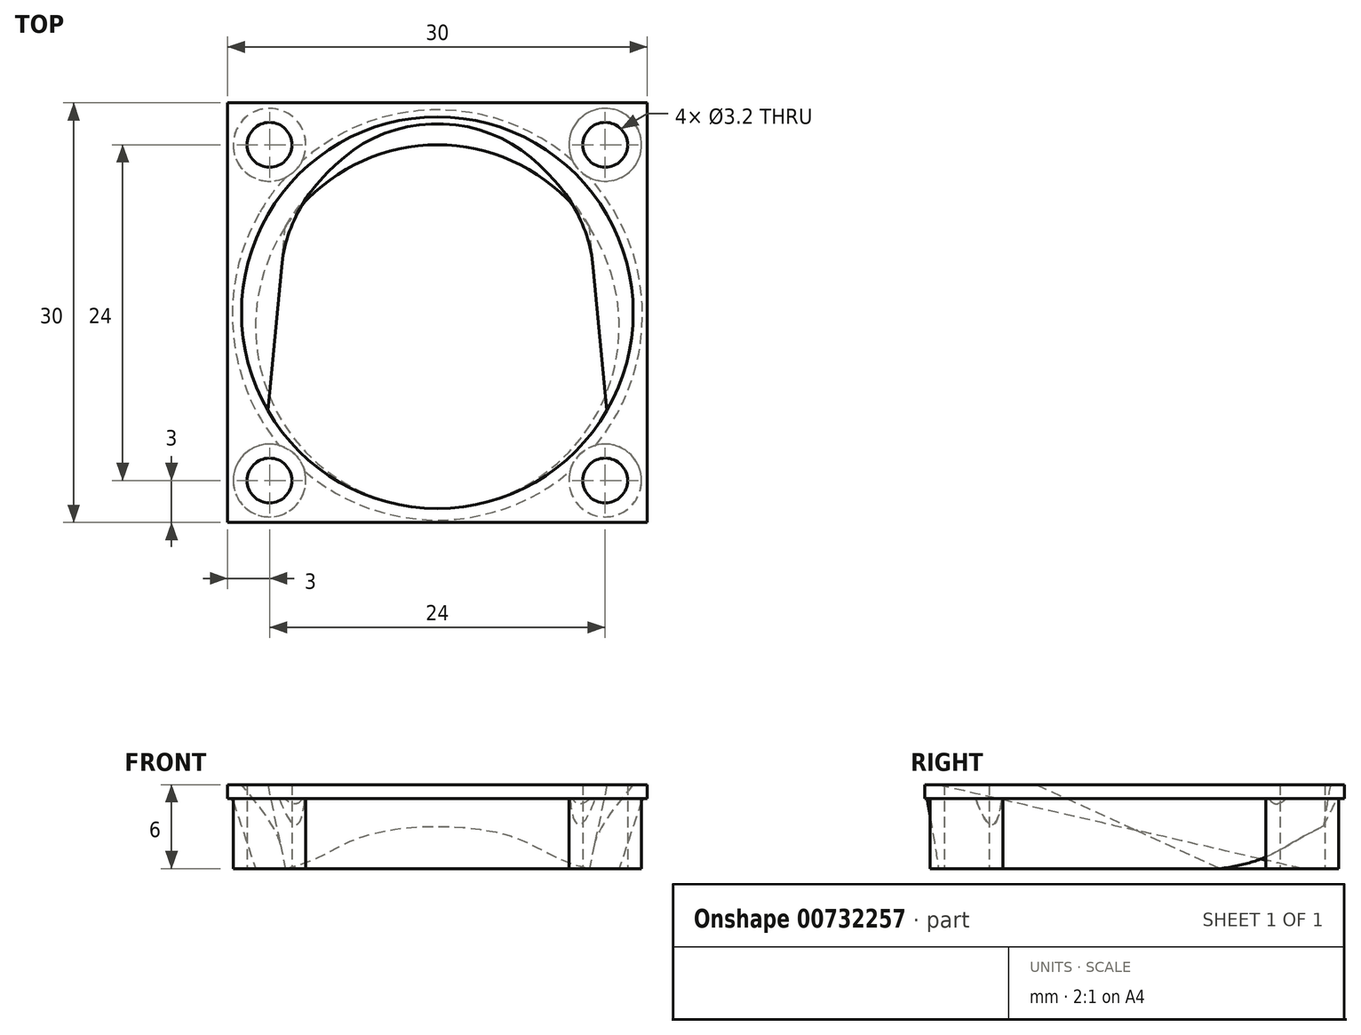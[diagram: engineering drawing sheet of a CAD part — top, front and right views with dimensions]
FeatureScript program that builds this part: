
annotation { "Feature Type Name" : "Feature", "Feature Type Description" : "" }
export const myFeature = defineFeature(function(context is Context, id is Id, definition is map)
    precondition{}
    {
        {
            var Q0;
            Q0=qCreatedBy(makeId("Top.planeOp"),FACE);
            var sketch = newSketch(context, id + "F0", { "sketchPlane" : qUnion([Q0])});
            skLineSegment(sketch, "E0.bottom", {"start": v(15, -15) * mm, "end": v(-15, -15) * mm});
            skLineSegment(sketch, "E0.top", {"start": v(15, 15) * mm, "end": v(-15, 15) * mm});
            skLineSegment(sketch, "E0.left", {"start": v(15, -15) * mm, "end": v(15, 15) * mm});
            skLineSegment(sketch, "E0.right", {"start": v(-15, -15) * mm, "end": v(-15, 15) * mm});
            skPoint(sketch, "E0.middle", {"position": v(0, 0) * mm});
            skLineSegment(sketch, "E1.bottom", {"start": v(12, -12) * mm, "end": v(-12, -12) * mm, "construction": true});
            skLineSegment(sketch, "E1.top", {"start": v(12, 12) * mm, "end": v(-12, 12) * mm, "construction": true});
            skLineSegment(sketch, "E1.left", {"start": v(12, -12) * mm, "end": v(12, 12) * mm, "construction": true});
            skLineSegment(sketch, "E1.right", {"start": v(-12, -12) * mm, "end": v(-12, 12) * mm, "construction": true});
            skCircle(sketch, "E2", {"center": v(-12, 12) * mm, "radius": 1.6 * mm});
            skCircle(sketch, "E3", {"center": v(12, 12) * mm, "radius": 1.6 * mm});
            skCircle(sketch, "E4", {"center": v(-12, -12) * mm, "radius": 1.6 * mm});
            skCircle(sketch, "E5", {"center": v(12, -12) * mm, "radius": 1.6 * mm});
            skSolve(sketch);
        }
        {
            var Q0;
            Q0=qSketchRegion(id+"F0",true);
            extrude(context, id + "F1", {"entities" : qUnion([Q0]), "depth" : 1 * mm, "offsetDistance" : 25 * mm});
        }
        {
            var Q0;
            Q0=makeQuery(id+"F1.opExtrude","CAP_FACE",FACE,{"disambiguationData":[OSD([sQuery(id+"F0.wireOp",EDGE,"E0.bottom"),sQuery(id+"F0.wireOp",EDGE,"E0.top"),sQuery(id+"F0.wireOp",EDGE,"E0.left"),sQuery(id+"F0.wireOp",EDGE,"E0.right"),sQuery(id+"F0.wireOp",EDGE,"E2"),sQuery(id+"F0.wireOp",EDGE,"E3"),sQuery(id+"F0.wireOp",EDGE,"E4"),sQuery(id+"F0.wireOp",EDGE,"E5")])],"isStart":true});
            var sketch = newSketch(context, id + "F2", { "sketchPlane" : qUnion([Q0])});
            skCircle(sketch, "E6", {"center": v(-12, 12) * mm, "radius": 2.6 * mm});
            skCircle(sketch, "E7.0", {"center": v(-12, 12) * mm, "radius": 1.6 * mm});
            skCircle(sketch, "E8.0", {"center": v(-12, -12) * mm, "radius": 1.6 * mm});
            skCircle(sketch, "E9", {"center": v(-12, -12) * mm, "radius": 2.6 * mm});
            skSolve(sketch);
        }
        {
            var Q0;
            Q0=qSketchRegion(id+"F2",true);
            extrude(context, id + "F3", {"entities" : qUnion([Q0]), "operationType" : NewBodyOperationType.ADD, "depth" : 5 * mm, "offsetDistance" : 25 * mm});
        }
        {
            var Q0;
            Q0=makeQuery(id+"F1.opExtrude","SWEPT_BODY",BODY,{"disambiguationData":[OSD([sQuery(id+"F0.wireOp",EDGE,"E0.bottom"),sQuery(id+"F0.wireOp",EDGE,"E0.top"),sQuery(id+"F0.wireOp",EDGE,"E0.left"),sQuery(id+"F0.wireOp",EDGE,"E0.right"),sQuery(id+"F0.wireOp",EDGE,"E2"),sQuery(id+"F0.wireOp",EDGE,"E3"),sQuery(id+"F0.wireOp",EDGE,"E4"),sQuery(id+"F0.wireOp",EDGE,"E5")])]});
            var Q1;
            Q1=qCreatedBy(makeId("Right.planeOp"),FACE);
            mirror(context, id + "F4", {"operationType" : NewBodyOperationType.ADD, "entities" : qUnion([Q0]), "mirrorPlane" : qUnion([Q1])});
        }
        {
            var Q0;
            Q0=makeQuery(id+"F3.opExtrude","CAP_FACE",FACE,{"disambiguationData":[OSD([sQuery(id+"F2.wireOp",EDGE,"E8.0"),sQuery(id+"F2.wireOp",EDGE,"E9")])],"isStart":false});
            var sketch = newSketch(context, id + "F5", { "sketchPlane" : qUnion([Q0])});
            skCircle(sketch, "E10", {"center": v(0, 1) * mm, "radius": 13 * mm});
            skSolve(sketch);
        }
        {
            var Q0;
            Q0=makeQuery(id+"F1.opExtrude","CAP_FACE",FACE,{"disambiguationData":[OSD([sQuery(id+"F0.wireOp",EDGE,"E0.bottom"),sQuery(id+"F0.wireOp",EDGE,"E0.top"),sQuery(id+"F0.wireOp",EDGE,"E0.left"),sQuery(id+"F0.wireOp",EDGE,"E0.right"),sQuery(id+"F0.wireOp",EDGE,"E2"),sQuery(id+"F0.wireOp",EDGE,"E3"),sQuery(id+"F0.wireOp",EDGE,"E4"),sQuery(id+"F0.wireOp",EDGE,"E5")])],"isStart":false});
            var sketch = newSketch(context, id + "F6", { "sketchPlane" : qUnion([Q0])});
            skCircle(sketch, "E11", {"center": v(0, 0) * mm, "radius": 15 * mm});
            skSolve(sketch);
        }
        {
            var Q0;
            Q0=qSketchRegion(id+"F5",true);
            var Q1;
            {var subQ0=sQuery(id+"F6.wireOp",EDGE,"E11");var subQ1=makeQuery(id+"F6.imprint","INTERSECT",VERTEX,{"derivedFrom":[makeQuery(id+"F1.opExtrude","CAP_EDGE",EDGE,{"disambiguationData":[OSD([sQuery(id+"F0.wireOp",EDGE,"E0.top")])],"isStart":false}),subQ0]});Q1=makeQuery(id+"F6.imprint","IMPRINT",FACE,{"disambiguationData":[TD([[makeQuery(id+"F6.imprint","IMPRINT",EDGE,{"disambiguationData":[TD([[subQ1,1.0]])],"derivedFrom":subQ0}),1.0]])]});}
            loft(context, id + "F7", {"operationType" : NewBodyOperationType.ADD, "sheetProfilesArray" : [{ "sheetProfileEntities" : qUnion([Q0]) }, { "sheetProfileEntities" : qUnion([Q1]) }]});
        }
        {
            var Q0;
            Q0=makeQuery(id+"F7.opLoft","CAP_FACE",FACE,{"disambiguationData":[OSD([makeQuery(id+"F5.imprint","IMPRINT",FACE,{"disambiguationData":[TD([[makeQuery(id+"F5.imprint","IMPRINT",EDGE,{"derivedFrom":sQuery(id+"F5.wireOp",EDGE,"E10")}),1.0]])]})])],"isStart":true});
            var sketch = newSketch(context, id + "F8", { "sketchPlane" : qUnion([Q0])});
            skFitSpline(sketch, "E12.0", {"points": [v(0, -13) * mm, v(0.4, -13) * mm, v(1.18, -12.96) * mm, v(2.35, -12.79) * mm, v(3.49, -12.5) * mm, v(4.6, -12.1) * mm, v(5.67, -11.6) * mm, v(6.68, -11) * mm, v(7.62, -10.3) * mm, v(8.5, -9.5) * mm, v(9.3, -8.63) * mm, v(10, -7.68) * mm, v(10.6, -6.67) * mm, v(11.1, -5.6) * mm, v(11.5, -4.49) * mm, v(11.79, -3.34) * mm, v(11.96, -2.18) * mm, v(12, -1.4) * mm, v(12, -1) * mm]});
            skFitSpline(sketch, "E12.1", {"points": [v(-12, -1) * mm, v(-12, -1.4) * mm, v(-11.96, -2.18) * mm, v(-11.79, -3.35) * mm, v(-11.5, -4.49) * mm, v(-11.1, -5.6) * mm, v(-10.6, -6.67) * mm, v(-10, -7.68) * mm, v(-9.3, -8.62) * mm, v(-8.5, -9.5) * mm, v(-7.63, -10.3) * mm, v(-6.68, -11) * mm, v(-5.67, -11.6) * mm, v(-4.6, -12.1) * mm, v(-3.49, -12.5) * mm, v(-2.34, -12.79) * mm, v(-1.18, -12.96) * mm, v(-0.4, -13) * mm, v(0, -13) * mm]});
            skFitSpline(sketch, "E12.2", {"points": [v(0, 11) * mm, v(-0.4, 11) * mm, v(-1.18, 10.96) * mm, v(-2.35, 10.79) * mm, v(-3.49, 10.5) * mm, v(-4.6, 10.1) * mm, v(-5.67, 9.6) * mm, v(-6.68, 9) * mm, v(-7.62, 8.3) * mm, v(-8.5, 7.5) * mm, v(-9.3, 6.63) * mm, v(-10, 5.68) * mm, v(-10.6, 4.67) * mm, v(-11.1, 3.6) * mm, v(-11.5, 2.49) * mm, v(-11.79, 1.34) * mm, v(-11.96, 0.18) * mm, v(-12, -0.6) * mm, v(-12, -1) * mm]});
            skFitSpline(sketch, "E12.3", {"points": [v(12, -1) * mm, v(12, -0.6) * mm, v(11.96, 0.18) * mm, v(11.79, 1.35) * mm, v(11.5, 2.49) * mm, v(11.1, 3.6) * mm, v(10.6, 4.67) * mm, v(10, 5.68) * mm, v(9.3, 6.62) * mm, v(8.5, 7.5) * mm, v(7.63, 8.3) * mm, v(6.68, 9) * mm, v(5.67, 9.6) * mm, v(4.6, 10.1) * mm, v(3.49, 10.5) * mm, v(2.34, 10.79) * mm, v(1.18, 10.96) * mm, v(0.4, 11) * mm, v(0, 11) * mm]});
            skSolve(sketch);
        }
        {
            var Q0;
            Q0=makeQuery(id+"F1.opExtrude","CAP_FACE",FACE,{"disambiguationData":[OSD([sQuery(id+"F0.wireOp",EDGE,"E0.bottom"),sQuery(id+"F0.wireOp",EDGE,"E0.top"),sQuery(id+"F0.wireOp",EDGE,"E0.left"),sQuery(id+"F0.wireOp",EDGE,"E0.right"),sQuery(id+"F0.wireOp",EDGE,"E2"),sQuery(id+"F0.wireOp",EDGE,"E3"),sQuery(id+"F0.wireOp",EDGE,"E4"),sQuery(id+"F0.wireOp",EDGE,"E5")])],"isStart":false});
            var sketch = newSketch(context, id + "F9", { "sketchPlane" : qUnion([Q0])});
            skCircle(sketch, "E13", {"center": v(0, 0) * mm, "radius": 14 * mm});
            skSolve(sketch);
        }
        {
            var Q1;
            Q1=makeQuery(id+"F9.imprint","IMPRINT",FACE,{"disambiguationData":[TD([[makeQuery(id+"F9.imprint","IMPRINT",EDGE,{"derivedFrom":sQuery(id+"F9.wireOp",EDGE,"E13")}),1.0]])]});
            var Q2;
            Q2=makeQuery(id+"F8.imprint","IMPRINT",FACE,{"disambiguationData":[TD([[makeQuery(id+"F8.imprint","IMPRINT",EDGE,{"derivedFrom":sQuery(id+"F8.wireOp",EDGE,"E12.0")}),1.0]])]});
            loft(context, id + "F10", {"operationType" : NewBodyOperationType.REMOVE, "sheetProfilesArray" : [{ "sheetProfileEntities" : qUnion([Q1]) }, { "sheetProfileEntities" : qUnion([Q2]) }]});
        }
    });
